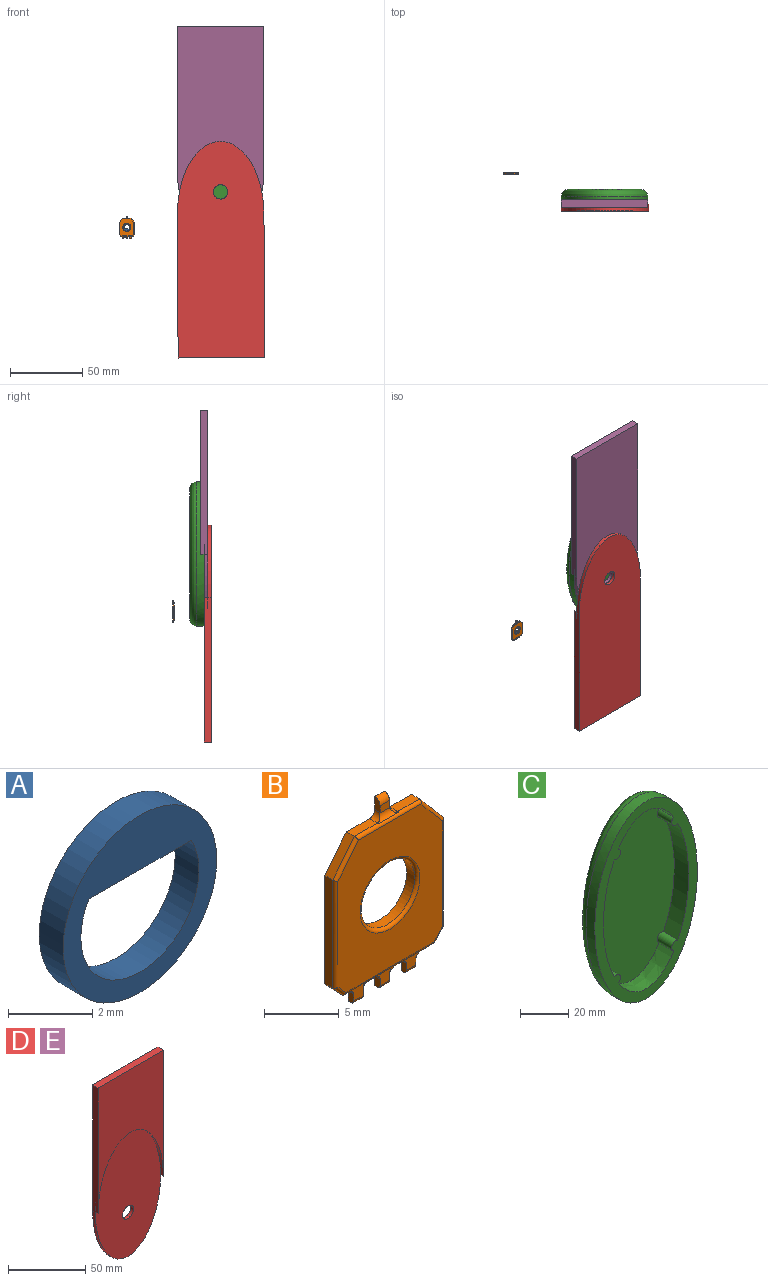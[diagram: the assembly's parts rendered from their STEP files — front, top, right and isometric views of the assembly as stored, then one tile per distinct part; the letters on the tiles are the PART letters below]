
ASSEMBLY  parts=5 mates=3
PART A: 5 faces, bbox 5.2x0.8x5.2 mm
  f0: cylinder r=1.98mm len=3.96mm, axis (0,1,0), area 6.6mm2, adj f1,f3,f4
  f1: plane 3.43x0.8mm, normal (0,0,-1), area 2.7mm2, adj f0,f3,f4
  f2: cylinder r=2.58mm len=5.15mm, axis (0,1,0), area 12.9mm2, adj f3,f4
  f3: plane 5.15x5.15mm, normal (0,-1,0), area 10.9mm2, adj f0,f1,f2
  f4: plane 5.15x5.15mm, normal (0,1,0), area 10.9mm2, adj f0,f1,f2
PART B: 74 faces, bbox 10.4x1x15.5 mm
  f0: plane 2.16x0.75mm, normal (0,0,1), area 1.6mm2, adj f33,f36,f48,f72
  f1: plane 0.9x0.25mm, normal (0,0,-1), area 0.2mm2, adj f7,f8,f36,f60
  f2: plane 0.9x0.25mm, normal (0,0,-1), area 0.2mm2, adj f13,f14,f36,f43
  f3: plane 0.9x0.25mm, normal (0,0,-1), area 0.2mm2, adj f19,f20,f36,f42
  f4: plane 1.05x0.5mm, normal (1,0,0), area 0.5mm2, adj f36,f41,f68,f69
  f5: plane 1.05x0.5mm, normal (-1,0,0), area 0.5mm2, adj f36,f41,f68,f72
  f6: plane 0.5x0.31mm, normal (-0.44,0,-0.9), area 0.2mm2, adj f25,f36,f40,f62
  f7: plane 0.84x0.5mm, normal (-1,0,0), area 0.4mm2, adj f1,f36,f40,f60,f62
  f8: plane 0.84x0.5mm, normal (1,0,0), area 0.4mm2, adj f1,f36,f40,f60,f63
  f9: plane 0.5x0.31mm, normal (0.44,0,-0.9), area 0.2mm2, adj f10,f36,f40,f63
  f10: plane 0.75x0.34mm, normal (1,0,0), area 0.2mm2, adj f9,f26,f36,f40,f46
  f11: plane 0.75x0.34mm, normal (-1,0,0), area 0.2mm2, adj f12,f26,f36,f39,f51
  f12: plane 0.5x0.31mm, normal (-0.44,0,-0.9), area 0.2mm2, adj f11,f36,f39,f64
  f13: plane 0.84x0.5mm, normal (-1,0,0), area 0.4mm2, adj f2,f36,f39,f43,f64
  f14: plane 0.84x0.5mm, normal (1,0,0), area 0.4mm2, adj f2,f36,f39,f43,f65
  f15: plane 0.5x0.31mm, normal (0.44,0,-0.9), area 0.2mm2, adj f16,f36,f39,f65
  f16: plane 0.75x0.34mm, normal (1,0,0), area 0.2mm2, adj f15,f27,f36,f39,f51
  f17: plane 0.75x0.34mm, normal (-1,0,0), area 0.2mm2, adj f18,f27,f36,f38,f59
  f18: plane 0.5x0.31mm, normal (-0.44,0,-0.9), area 0.2mm2, adj f17,f36,f38,f66
  f19: plane 0.84x0.5mm, normal (-1,0,0), area 0.4mm2, adj f3,f36,f38,f42,f66
  f20: plane 0.84x0.5mm, normal (1,0,0), area 0.4mm2, adj f3,f36,f38,f42,f67
  f21: plane 0.5x0.31mm, normal (0.44,0,-0.9), area 0.2mm2, adj f22,f36,f38,f67
  f22: plane 0.75x0.34mm, normal (1,0,0), area 0.2mm2, adj f21,f28,f36,f38,f59
  f23: plane 11.9x9.86mm, normal (0,-1,0), area 86.9mm2, adj f44,f45,f47,f48,f49,f50,f52,f53
  f24: plane 0.89x0.75mm, normal (0,0,-1), area 0.7mm2, adj f25,f35,f36,f49
  f25: plane 0.75x0.34mm, normal (-1,0,0), area 0.2mm2, adj f6,f24,f36,f40,f46
  f26: plane 0.75x0.7mm, normal (0,0,-1), area 0.5mm2, adj f10,f11,f36,f52
  f27: plane 0.75x0.7mm, normal (0,0,-1), area 0.5mm2, adj f16,f17,f36,f56
  f28: plane 0.89x0.75mm, normal (0,0,-1), area 0.7mm2, adj f22,f29,f36,f57
  f29: plane 0.99x0.89mm, normal (0.75,0,-0.67), area 1mm2, adj f28,f30,f36,f55
  f30: plane 8.87x0.75mm, normal (1,0,0), area 6.7mm2, adj f29,f31,f36,f53
  f31: plane 2.54x2.14mm, normal (0.76,0,0.64), area 2.5mm2, adj f30,f32,f36,f50
  f32: plane 2.08x0.75mm, normal (0,0,1), area 1.6mm2, adj f31,f36,f48,f69
  f33: plane 2.56x2.06mm, normal (-0.78,0,0.63), area 2.5mm2, adj f0,f34,f36,f45
  f34: plane 8.85x0.75mm, normal (-1,0,0), area 6.6mm2, adj f33,f35,f36,f44
  f35: plane 0.99x0.89mm, normal (-0.74,0,-0.67), area 1mm2, adj f24,f34,f36,f47
  f36: plane 15.52x10.36mm, normal (0,1,0), area 108.3mm2, adj f0,f1,f2,f3,f4,f5,f6,f7
  f37: cylinder r=2.58mm len=5.15mm, axis (0,-1,0), area 12.1mm2, adj f36,f61
  f38: plane 1.8x1.06mm, normal (0,-1,0), area 1.1mm2, adj f17,f18,f19,f20,f21,f22,f42,f59
  f39: plane 1.8x1.06mm, normal (0,-1,0), area 1.1mm2, adj f11,f12,f13,f14,f15,f16,f43,f51
  f40: plane 1.8x1.06mm, normal (0,-1,0), area 1.1mm2, adj f6,f7,f8,f9,f10,f25,f46,f60
  f41: plane 0.9x0.59mm, normal (0,-1,0), area 0.5mm2, adj f4,f5,f68,f69,f72,f73
  f42: cylinder r=0.25mm len=0.9mm, axis (-1,0,0), area 0.4mm2, adj f3,f19,f20,f38
  f43: cylinder r=0.25mm len=0.9mm, axis (-1,0,0), area 0.4mm2, adj f2,f13,f14,f39
  f44: cylinder r=0.25mm len=8.85mm, axis (0,0,1), area 3.4mm2, adj f23,f34,f45,f47
  f45: cylinder r=0.25mm len=2.71mm, axis (0.63,0,0.78), area 1.2mm2, adj f23,f33,f44,f48
  f46: cylinder r=0.25mm len=1.8mm, axis (1,0,0), area 0.7mm2, adj f10,f25,f40,f49
  f47: cylinder r=0.25mm len=1.16mm, axis (-0.67,0,0.74), area 0.5mm2, adj f23,f35,f44,f49
  f48: cylinder r=0.25mm len=6.16mm, axis (1,0,0), area 2.2mm2, adj f0,f23,f32,f45,f50,f70,f71,f73
  f49: cylinder r=0.25mm len=2.69mm, axis (-1,0,0), area 1mm2, adj f23,f24,f46,f47,f52
  f50: cylinder r=0.25mm len=2.7mm, axis (0.64,0,-0.76), area 1.3mm2, adj f23,f31,f48,f53
  f51: cylinder r=0.25mm len=1.8mm, axis (-1,0,0), area 0.7mm2, adj f11,f16,f39,f54
  f52: cylinder r=0.25mm len=0.7mm, axis (-1,0,0), area 0.3mm2, adj f23,f26,f49,f54
  f53: cylinder r=0.25mm len=8.87mm, axis (0,0,-1), area 3.4mm2, adj f23,f30,f50,f55
  f54: cylinder r=0.25mm len=1.8mm, axis (-1,0,0), area 0.7mm2, adj f23,f51,f52,f56
  f55: cylinder r=0.25mm len=1.16mm, axis (-0.67,0,-0.75), area 0.5mm2, adj f23,f29,f53,f57
  f56: cylinder r=0.25mm len=0.7mm, axis (-1,0,0), area 0.3mm2, adj f23,f27,f54,f58
  f57: cylinder r=0.25mm len=0.89mm, axis (-1,0,0), area 0.3mm2, adj f23,f28,f55,f58
  f58: cylinder r=0.25mm len=1.8mm, axis (-1,0,0), area 0.7mm2, adj f23,f56,f57,f59
  f59: cylinder r=0.25mm len=1.8mm, axis (-1,0,0), area 0.7mm2, adj f17,f22,f38,f58
  f60: cylinder r=0.25mm len=0.9mm, axis (-1,0,0), area 0.4mm2, adj f1,f7,f8,f40
  f61: torus R=2.82mm, axis (0,-1,0), area 6.6mm2, adj f23,f37
  f62: cylinder r=0.25mm len=0.5mm, axis (0,1,0), area 0.1mm2, adj f6,f7,f36,f40
  f63: cylinder r=0.25mm len=0.5mm, axis (0,1,0), area 0.1mm2, adj f8,f9,f36,f40
  f64: cylinder r=0.25mm len=0.5mm, axis (0,-1,0), area 0.1mm2, adj f12,f13,f36,f39
  f65: cylinder r=0.25mm len=0.5mm, axis (0,-1,0), area 0.1mm2, adj f14,f15,f36,f39
  f66: cylinder r=0.25mm len=0.5mm, axis (0,1,0), area 0.1mm2, adj f18,f19,f36,f38
  f67: cylinder r=0.25mm len=0.5mm, axis (0,-1,0), area 0.1mm2, adj f20,f21,f36,f38
  f68: cylinder r=0.51mm len=0.9mm, axis (-1,0,0), area 0.7mm2, adj f4,f5,f36,f41
  f69: cylinder r=0.51mm len=0.75mm, axis (0,-1,0), area 0.5mm2, adj f4,f32,f36,f41,f70,f73
  f70: torus R=0.76mm, axis (1,0,0), area 0mm2, adj f48,f69,f73
  f71: torus R=0.76mm, axis (1,0,0), area 0mm2, adj f48,f72,f73
  f72: cylinder r=0.51mm len=0.75mm, axis (0,1,0), area 0.5mm2, adj f0,f5,f36,f41,f71,f73
  f73: cylinder r=0.51mm len=1.92mm, axis (1,0,0), area 0.8mm2, adj f41,f48,f69,f70,f71,f72
PART C: 13 faces, bbox 60x10x100 mm
  f0: plane 100x60mm, normal (0,-1,0), area 1236.6mm2, adj f1,f3,f4,f5,f6,f7,f8,f9
  f1: extruded ~100x60mm, area 1276.4mm2, adj f0,f12
  f2: plane 90.01x50.01mm, normal (0,1,0), area 3514.5mm2, adj f12
  f3: cylinder r=2.5mm len=8.5mm, axis (0,-1,0), area 65.5mm2, adj f0,f4,f10,f11
  f4: extruded ~32.4x11.05mm, area 347.3mm2, adj f0,f3,f5,f11
  f5: cylinder r=2.5mm len=8.5mm, axis (0,-1,0), area 65.5mm2, adj f0,f4,f6,f11
  f6: extruded ~59.2x8.5mm, area 519mm2, adj f0,f5,f7,f11
  f7: cylinder r=2.5mm len=8.5mm, axis (0,-1,0), area 65.5mm2, adj f0,f6,f8,f11
  f8: extruded ~32.4x11.05mm, area 347.3mm2, adj f0,f7,f9,f11
  f9: cylinder r=2.5mm len=8.5mm, axis (0,-1,0), area 65.5mm2, adj f0,f8,f10,f11
  f10: extruded ~59.2x8.5mm, area 519mm2, adj f0,f3,f9,f11
  f11: plane 90x50mm, normal (0,-1,0), area 3475.8mm2, adj f3,f4,f5,f6,f7,f8,f9,f10
  f12: bspline ~100.01x60.01mm, area 1915.4mm2, adj f1,f2
PART D: 9 faces, bbox 60x5x150 mm
  f0: extruded ~60x50mm, area 319.1mm2, adj f1,f3,f5,f7
  f1: plane 100x5mm, normal (1,0,0), area 500mm2, adj f0,f2,f4,f5,f6
  f2: plane 60x5mm, normal (0,0,1), area 300mm2, adj f1,f3,f4,f5
  f3: plane 100x5mm, normal (-1,0,0), area 500mm2, adj f0,f2,f4,f5,f6
  f4: plane 100x60mm, normal (0,-1,0), area 3643.8mm2, adj f1,f2,f3,f6
  f5: plane 150x60mm, normal (0,1,0), area 8277.7mm2, adj f0,f1,f2,f3,f8
  f6: extruded ~60x50mm, area 319.1mm2, adj f1,f3,f4,f7
  f7: plane 100x60mm, normal (0,-1,0), area 4633.9mm2, adj f0,f6,f8
  f8: cylinder r=5mm len=10mm, axis (0,-1,0), area 78.5mm2, adj f5,f7
PART E: same geometry as D
PLACE A rot(axis=(0,-1,0),176.1deg) t=(-87.01,0.6,44.67)mm
PLACE B t=(-87.01,0.58,44.67)mm fixed
PLACE C t=(-22.03,-11.06,84.53)mm
PLACE D rot(axis=(1,0,0),180deg) t=(-21.71,-26.06,4.27)mm
PLACE E rot(axis=(0,0,-1),180deg) t=(-22.03,-23.56,134.27)mm fixed
MATE fastened C.f0 <-> E.f7  axis (0,-1,0) through (-22.03,-21.06,84.53)mm
MATE revolute A.f2 <-> B.f37  axis (0,1,0) through (-87.01,0.2,44.67)mm
MATE revolute D.f8 <-> E.f8  axis (0,1,0) through (-22.03,-23.56,69.27)mm
